# Revit family: Legrand_Coffret_résidentiel_Drivia_13_modules
name_source: partatom
category: Equipement électrique
revit_build: Autodesk Revit 2018 (Build: 20170223_1515(x64)
units: mm (PartAtom-declared; Revit-internal decimal feet)

## family parameters
Basée sur le plan de construction = Non
Configuration du panneau = Deux colonnes, circuits au sein
Cote de connecteur circulaire = Utiliser le diamètre
Couper avec des vides une fois chargée = Non
Numéro OmniClass = 23.80.30.11.17
Partagée = Non
Point de calcul de pièce = Non
Titre OmniClass = Distribution Boards and Control Panels
Toujours verticalement = Oui
Type d'élément = Tableau de raccordement

## types (4) — shared parameters
Conditions Générale d'Utilisation = https://export.legrand.com
ETIM Class 6.0 = EC000214
Fabricant = Legrand
ICC = 10000 A
IK = 05
IP = 30
Largeur = 250 mm  [stored 0.82021 ft]
Largeur zone d'installation = 750 mm  [stored 2.46063 ft]
Matière = polystyréne choc
RAL = 9003
Tension = 400V AC - 50/60 Hz
UIMP = 6000 V
URL = www.legrand.fr
autoextinguibilité = 750 °C
distance avant zone d'installation = 104 mm
distance coté zone d'installation = 250 mm  [stored 0.82021 ft]
porte blanche = Non
porte blanche 401331 = Non
porte blanche 401332 = Non
porte blanche 401333 = Non
porte blanche 401334 = Non
porte transparente = Non
porte transparente 401341 = Non
porte transparente 401342 = Non
porte transparente 401343 = Non
porte transparente 401344 = Non
profondeur = 104 mm
profondeur zone d'installation = 207 mm  [stored 0.679134 ft]

## per-type parameters (varying)
| type | Coffret 401211 | Coffret 401212 | Coffret 401213 | Coffret 401214 | Description | Hauteur | Image du type | courant max admissible |
| Legrand Coffret résidentiel Drivia plastique 1 rangée 13 modules | Oui | Non | Non | Non | 401211 Legrand Coffret résidentiel Drivia plastique 1 rangée 13 modules | 250 mm  [stored 0.82021 ft] | Drivia_1rangee_13m_401211_pw_206357_pz_1.jpg | 60 A |
| Legrand Coffret résidentiel Drivia plastique 2 rangées 13 modules | Non | Oui | Non | Non | 401212 Legrand Coffret résidentiel Drivia plastique 2 rangées 13 modules | 375 mm  [stored 1.23031 ft] | Drivia_2rangee_13m_401211_pw_206357_pz_1.jpg | 90 A |
| Legrand Coffret résidentiel Drivia plastique 3 rangées 13 modules | Non | Non | Oui | Non | 401213 Legrand Coffret résidentiel Drivia plastique 3 rangées 13 modules | 500 mm  [stored 1.64042 ft] | Drivia_3rangees_401213_pw_206551_pz_1.jpg | 90 A |
| Legrand Coffret résidentiel Drivia plastique 4 rangées 13 modules | Non | Non | Non | Oui | 401214 Legrand Coffret résidentiel Drivia plastique 4 rangées 13 modules | 625 mm  [stored 2.05052 ft] | Drivia_4rangees_13m_401211_pw_206357_pz_1.jpg | 90 A |

note: [stored X ft] marks values corroborated as IEEE doubles in the binary element streams (Revit-internal decimal feet)
